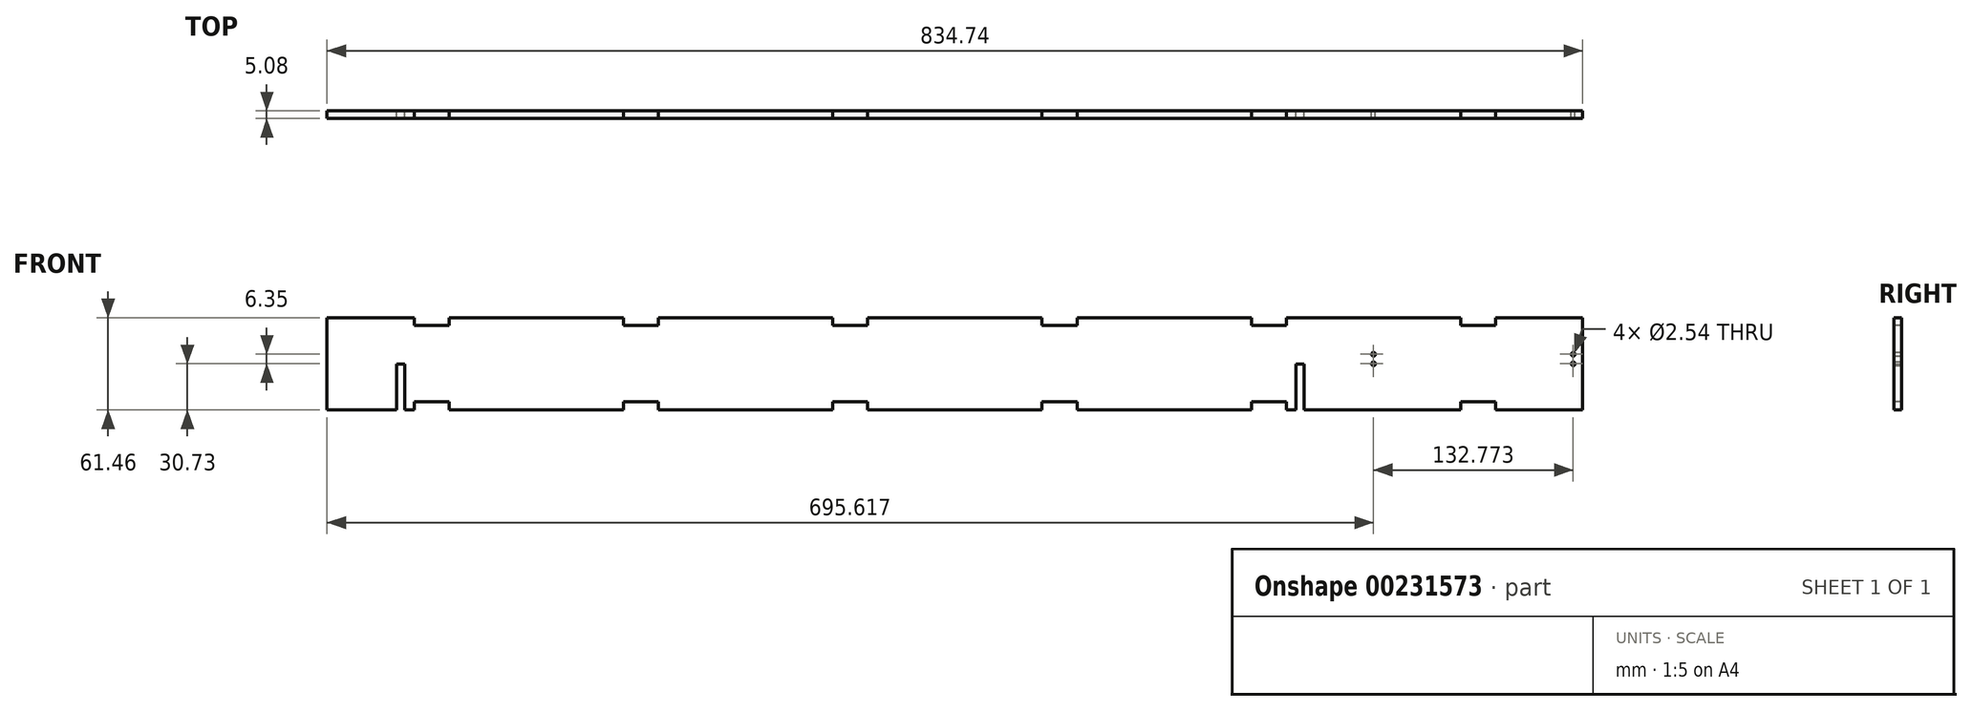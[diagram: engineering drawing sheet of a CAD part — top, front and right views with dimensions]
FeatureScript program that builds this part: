
annotation { "Feature Type Name" : "Feature", "Feature Type Description" : "" }
export const myFeature = defineFeature(function(context is Context, id is Id, definition is map)
    precondition{}
    {
        {
            var Q0;
            Q0=qCreatedBy(makeId("Front.planeOp"),FACE);
            var sketch = newSketch(context, id + "F0", { "sketchPlane" : qUnion([Q0])});
            skLineSegment(sketch, "E0.bottom", {"start": v(0, 0) * mm, "end": v(834.74, 0) * mm});
            skLineSegment(sketch, "E0.top", {"start": v(0, 50.8) * mm, "end": v(834.74, 50.8) * mm});
            skLineSegment(sketch, "E0.left", {"start": v(0, 0) * mm, "end": v(0, 50.8) * mm});
            skLineSegment(sketch, "E0.right", {"start": v(834.74, 0) * mm, "end": v(834.74, 50.8) * mm});
            skLineSegment(sketch, "E1", {"start": v(57.92, 50.8) * mm, "end": v(57.92, 0) * mm, "construction": true});
            skLineSegment(sketch, "E2", {"start": v(75.88, 50.8) * mm, "end": v(75.88, 0) * mm, "construction": true});
            skLineSegment(sketch, "E3", {"start": v(776.82, 50.8) * mm, "end": v(776.82, 0) * mm, "construction": true});
            skLineSegment(sketch, "E4", {"start": v(758.86, 50.8) * mm, "end": v(758.86, 0) * mm, "construction": true});
            skSolve(sketch);
        }
        {
            var Q0;
            Q0=makeQuery(id+"F0.imprint","IMPRINT",FACE,{"disambiguationData":[TD([[makeQuery(id+"F0.imprint","IMPRINT",EDGE,{"derivedFrom":sQuery(id+"F0.wireOp",EDGE,"E0.bottom")}),1.0]])]});
            extrude(context, id + "F1", {"entities" : qUnion([Q0]), "depth" : 5.08 * mm});
        }
        {
            var Q0;
            Q0=makeQuery(id+"F1.opExtrude","CAP_FACE",FACE,{"disambiguationData":[OSD([sQuery(id+"F0.wireOp",EDGE,"E0.bottom"),sQuery(id+"F0.wireOp",EDGE,"E0.top"),sQuery(id+"F0.wireOp",EDGE,"E0.left"),sQuery(id+"F0.wireOp",EDGE,"E0.right")])],"isStart":false});
            var sketch = newSketch(context, id + "F2", { "sketchPlane" : qUnion([Q0])});
            skLineSegment(sketch, "E5", {"start": v(57.92, 0) * mm, "end": v(57.92, 50.8) * mm});
            skLineSegment(sketch, "E6", {"start": v(81.2, 0) * mm, "end": v(81.2, 50.8) * mm});
            skLineSegment(sketch, "E7", {"start": v(776.82, 0) * mm, "end": v(776.82, 50.8) * mm});
            skLineSegment(sketch, "E8", {"start": v(753.54, 0) * mm, "end": v(753.54, 50.8) * mm});
            skLineSegment(sketch, "E9", {"start": v(197.05, 50.8) * mm, "end": v(197.05, 0) * mm});
            skLineSegment(sketch, "E10", {"start": v(220.32, 0) * mm, "end": v(220.32, 50.8) * mm});
            skLineSegment(sketch, "E11", {"start": v(336.17, 50.8) * mm, "end": v(336.17, 0) * mm});
            skLineSegment(sketch, "E12", {"start": v(359.45, 0.94) * mm, "end": v(359.45, 50.8) * mm});
            skLineSegment(sketch, "E13", {"start": v(475.3, 0) * mm, "end": v(475.3, 50.8) * mm});
            skLineSegment(sketch, "E14", {"start": v(498.57, 0) * mm, "end": v(498.57, 50.8) * mm});
            skLineSegment(sketch, "E15", {"start": v(614.42, 50.8) * mm, "end": v(614.42, 0) * mm});
            skLineSegment(sketch, "E16", {"start": v(637.7, 50.8) * mm, "end": v(637.7, 0) * mm});
            skCircle(sketch, "E17", {"center": v(9.53, 25.4) * mm, "radius": 1.27 * mm});
            skPoint(sketch, "E17.centerSnap0", {"position": v(0, 25.4) * mm});
            skCircle(sketch, "E18", {"center": v(825.22, 25.4) * mm, "radius": 1.27 * mm});
            skSolve(sketch);
        }
        {
            var Q0;
            {var subQ0=sQuery(id+"F2.wireOp",EDGE,"E6");Q0=makeQuery(id+"F2.imprint","IMPRINT",FACE,{"disambiguationData":[TD([[makeQuery(id+"F2.imprint","IMPRINT",EDGE,{"derivedFrom":subQ0}),-1.0]])]});}
            var sketch = newSketch(context, id + "F3", { "sketchPlane" : qUnion([Q0])});
            skLineSegment(sketch, "E19", {"start": v(0, 25.4) * mm, "end": v(834.74, 25.4) * mm, "construction": true});
            skLineSegment(sketch, "E20", {"start": v(0, 50.8) * mm, "end": v(0, 56.13) * mm});
            skLineSegment(sketch, "E21", {"start": v(0, 56.13) * mm, "end": v(57.92, 56.13) * mm});
            skLineSegment(sketch, "E22", {"start": v(57.92, 56.13) * mm, "end": v(57.92, 50.8) * mm});
            skLineSegment(sketch, "E23", {"start": v(81.2, 50.8) * mm, "end": v(81.2, 56.13) * mm});
            skLineSegment(sketch, "E24", {"start": v(81.2, 56.13) * mm, "end": v(197.05, 56.13) * mm});
            skLineSegment(sketch, "E25", {"start": v(197.05, 56.13) * mm, "end": v(197.05, 50.8) * mm});
            skLineSegment(sketch, "E26", {"start": v(220.32, 50.8) * mm, "end": v(220.32, 56.13) * mm});
            skLineSegment(sketch, "E27", {"start": v(220.32, 56.13) * mm, "end": v(336.17, 56.13) * mm});
            skLineSegment(sketch, "E28", {"start": v(336.17, 56.13) * mm, "end": v(336.17, 50.8) * mm});
            skLineSegment(sketch, "E29", {"start": v(359.45, 50.8) * mm, "end": v(359.45, 56.13) * mm});
            skLineSegment(sketch, "E30", {"start": v(359.45, 56.13) * mm, "end": v(475.3, 56.13) * mm});
            skLineSegment(sketch, "E31", {"start": v(475.3, 56.13) * mm, "end": v(475.3, 50.8) * mm});
            skLineSegment(sketch, "E32", {"start": v(498.57, 50.8) * mm, "end": v(498.57, 56.13) * mm});
            skLineSegment(sketch, "E33", {"start": v(498.57, 56.13) * mm, "end": v(614.42, 56.13) * mm});
            skLineSegment(sketch, "E34", {"start": v(614.42, 56.13) * mm, "end": v(614.42, 50.8) * mm});
            skLineSegment(sketch, "E35", {"start": v(637.7, 50.8) * mm, "end": v(637.7, 56.13) * mm});
            skLineSegment(sketch, "E36", {"start": v(637.7, 56.13) * mm, "end": v(753.54, 56.13) * mm});
            skLineSegment(sketch, "E37", {"start": v(753.54, 56.13) * mm, "end": v(753.54, 50.8) * mm});
            skLineSegment(sketch, "E38", {"start": v(776.82, 50.8) * mm, "end": v(776.82, 56.13) * mm});
            skLineSegment(sketch, "E39", {"start": v(776.82, 56.13) * mm, "end": v(834.74, 56.13) * mm});
            skLineSegment(sketch, "E40", {"start": v(834.74, 56.13) * mm, "end": v(834.74, 50.8) * mm});
            skLineSegment(sketch, "E41.MirrorCS", {"start": v(637.7, 0) * mm, "end": v(637.7, -5.33) * mm});
            skLineSegment(sketch, "E42.MirrorCS", {"start": v(753.54, -5.33) * mm, "end": v(753.54, 0) * mm});
            skLineSegment(sketch, "E43.MirrorCS", {"start": v(498.57, 0) * mm, "end": v(498.57, -5.33) * mm});
            skLineSegment(sketch, "E44.MirrorCS", {"start": v(57.92, -5.33) * mm, "end": v(57.92, 0) * mm});
            skLineSegment(sketch, "E45.MirrorCS", {"start": v(776.82, 0) * mm, "end": v(776.82, -5.33) * mm});
            skLineSegment(sketch, "E46.MirrorCS", {"start": v(475.3, -5.33) * mm, "end": v(475.3, 0) * mm});
            skLineSegment(sketch, "E47.MirrorCS", {"start": v(81.2, 0) * mm, "end": v(81.2, -5.33) * mm});
            skLineSegment(sketch, "E48.MirrorCS", {"start": v(197.05, -5.33) * mm, "end": v(197.05, 0) * mm});
            skLineSegment(sketch, "E49.MirrorCS", {"start": v(614.42, -5.33) * mm, "end": v(614.42, 0) * mm});
            skLineSegment(sketch, "E50.MirrorCS", {"start": v(220.32, 0) * mm, "end": v(220.32, -5.33) * mm});
            skLineSegment(sketch, "E51.MirrorCS", {"start": v(359.45, 0) * mm, "end": v(359.45, -5.33) * mm});
            skLineSegment(sketch, "E52.MirrorCS", {"start": v(336.17, -5.33) * mm, "end": v(336.17, 0) * mm});
            skLineSegment(sketch, "E53.MirrorCS", {"start": v(0, 0) * mm, "end": v(0, -5.33) * mm});
            skLineSegment(sketch, "E54.MirrorCS", {"start": v(834.74, -5.33) * mm, "end": v(834.74, 0) * mm});
            skLineSegment(sketch, "E55.MirrorCS", {"start": v(776.82, -5.33) * mm, "end": v(834.74, -5.33) * mm});
            skLineSegment(sketch, "E56.MirrorCS", {"start": v(637.7, -5.33) * mm, "end": v(753.54, -5.33) * mm});
            skLineSegment(sketch, "E57.MirrorCS", {"start": v(498.57, -5.33) * mm, "end": v(614.42, -5.33) * mm});
            skLineSegment(sketch, "E58.MirrorCS", {"start": v(0, -5.33) * mm, "end": v(57.92, -5.33) * mm});
            skLineSegment(sketch, "E59.MirrorCS", {"start": v(81.2, -5.33) * mm, "end": v(197.05, -5.33) * mm});
            skLineSegment(sketch, "E60.MirrorCS", {"start": v(220.32, -5.33) * mm, "end": v(336.17, -5.33) * mm});
            skLineSegment(sketch, "E61.MirrorCS", {"start": v(359.45, -5.33) * mm, "end": v(475.3, -5.33) * mm});
            skLineSegment(sketch, "E62", {"start": v(0, 50.8) * mm, "end": v(834.74, 50.8) * mm});
            skLineSegment(sketch, "E63", {"start": v(834.74, 0) * mm, "end": v(0, 0) * mm});
            skSolve(sketch);
        }
        {
            var Q0;
            {var subQ0=sQuery(id+"F3.wireOp",EDGE,"E20");Q0=makeQuery(id+"F3.imprint","IMPRINT",FACE,{"disambiguationData":[TD([[makeQuery(id+"F3.imprint","IMPRINT",EDGE,{"derivedFrom":subQ0}),-1.0]])]});}
            var Q1;
            {var subQ0=sQuery(id+"F3.wireOp",EDGE,"E23");Q1=makeQuery(id+"F3.imprint","IMPRINT",FACE,{"disambiguationData":[TD([[makeQuery(id+"F3.imprint","IMPRINT",EDGE,{"derivedFrom":subQ0}),-1.0]])]});}
            var Q2;
            {var subQ0=sQuery(id+"F3.wireOp",EDGE,"E44.MirrorCS");Q2=makeQuery(id+"F3.imprint","IMPRINT",FACE,{"disambiguationData":[TD([[makeQuery(id+"F3.imprint","IMPRINT",EDGE,{"derivedFrom":subQ0}),1.0]])]});}
            var Q3;
            {var subQ0=sQuery(id+"F3.wireOp",EDGE,"E47.MirrorCS");Q3=makeQuery(id+"F3.imprint","IMPRINT",FACE,{"disambiguationData":[TD([[makeQuery(id+"F3.imprint","IMPRINT",EDGE,{"derivedFrom":subQ0}),1.0]])]});}
            var Q4;
            {var subQ0=sQuery(id+"F3.wireOp",EDGE,"E26");Q4=makeQuery(id+"F3.imprint","IMPRINT",FACE,{"disambiguationData":[TD([[makeQuery(id+"F3.imprint","IMPRINT",EDGE,{"derivedFrom":subQ0}),-1.0]])]});}
            var Q5;
            {var subQ0=sQuery(id+"F3.wireOp",EDGE,"E50.MirrorCS");Q5=makeQuery(id+"F3.imprint","IMPRINT",FACE,{"disambiguationData":[TD([[makeQuery(id+"F3.imprint","IMPRINT",EDGE,{"derivedFrom":subQ0}),1.0]])]});}
            var Q6;
            {var subQ0=sQuery(id+"F3.wireOp",EDGE,"E29");Q6=makeQuery(id+"F3.imprint","IMPRINT",FACE,{"disambiguationData":[TD([[makeQuery(id+"F3.imprint","IMPRINT",EDGE,{"derivedFrom":subQ0}),-1.0]])]});}
            var Q7;
            {var subQ0=sQuery(id+"F3.wireOp",EDGE,"E46.MirrorCS");Q7=makeQuery(id+"F3.imprint","IMPRINT",FACE,{"disambiguationData":[TD([[makeQuery(id+"F3.imprint","IMPRINT",EDGE,{"derivedFrom":subQ0}),1.0]])]});}
            var Q8;
            {var subQ0=sQuery(id+"F3.wireOp",EDGE,"E32");Q8=makeQuery(id+"F3.imprint","IMPRINT",FACE,{"disambiguationData":[TD([[makeQuery(id+"F3.imprint","IMPRINT",EDGE,{"derivedFrom":subQ0}),-1.0]])]});}
            var Q9;
            {var subQ0=sQuery(id+"F3.wireOp",EDGE,"E43.MirrorCS");Q9=makeQuery(id+"F3.imprint","IMPRINT",FACE,{"disambiguationData":[TD([[makeQuery(id+"F3.imprint","IMPRINT",EDGE,{"derivedFrom":subQ0}),1.0]])]});}
            var Q10;
            {var subQ0=sQuery(id+"F3.wireOp",EDGE,"E35");Q10=makeQuery(id+"F3.imprint","IMPRINT",FACE,{"disambiguationData":[TD([[makeQuery(id+"F3.imprint","IMPRINT",EDGE,{"derivedFrom":subQ0}),-1.0]])]});}
            var Q11;
            {var subQ0=sQuery(id+"F3.wireOp",EDGE,"E41.MirrorCS");Q11=makeQuery(id+"F3.imprint","IMPRINT",FACE,{"disambiguationData":[TD([[makeQuery(id+"F3.imprint","IMPRINT",EDGE,{"derivedFrom":subQ0}),1.0]])]});}
            var Q12;
            {var subQ0=sQuery(id+"F3.wireOp",EDGE,"E38");Q12=makeQuery(id+"F3.imprint","IMPRINT",FACE,{"disambiguationData":[TD([[makeQuery(id+"F3.imprint","IMPRINT",EDGE,{"derivedFrom":subQ0}),-1.0]])]});}
            var Q13;
            {var subQ0=sQuery(id+"F3.wireOp",EDGE,"E45.MirrorCS");Q13=makeQuery(id+"F3.imprint","IMPRINT",FACE,{"disambiguationData":[TD([[makeQuery(id+"F3.imprint","IMPRINT",EDGE,{"derivedFrom":subQ0}),1.0]])]});}
            extrude(context, id + "F4", {"entities" : qUnion([Q0, Q1, Q2, Q3, Q4, Q5, Q6, Q7, Q8, Q9, Q10, Q11, Q12, Q13]), "operationType" : NewBodyOperationType.ADD, "oppositeDirection" : true, "depth" : 5.08 * mm});
        }
        {
            var Q0;
            {var subQ0=sQuery(id+"F3.wireOp",EDGE,"E63");var subQ1=sQuery(id+"F3.wireOp",EDGE,"E62");Q0=makeQuery(id+"F4.boolean.opBoolean","MERGE",FACE,{"derivedFrom":[makeQuery(id+"F1.opExtrude","CAP_FACE",FACE,{"disambiguationData":[OSD([sQuery(id+"F0.wireOp",EDGE,"E0.bottom"),sQuery(id+"F0.wireOp",EDGE,"E0.top"),sQuery(id+"F0.wireOp",EDGE,"E0.left"),sQuery(id+"F0.wireOp",EDGE,"E0.right")])],"isStart":true}),makeQuery(id+"F4.opExtrude","CAP_FACE",FACE,{"disambiguationData":[OSD([sQuery(id+"F3.wireOp",EDGE,"E20"),sQuery(id+"F3.wireOp",EDGE,"E21"),sQuery(id+"F3.wireOp",EDGE,"E22"),subQ1])],"isStart":false}),makeQuery(id+"F4.opExtrude","CAP_FACE",FACE,{"disambiguationData":[OSD([sQuery(id+"F3.wireOp",EDGE,"E23"),sQuery(id+"F3.wireOp",EDGE,"E24"),sQuery(id+"F3.wireOp",EDGE,"E25"),subQ1])],"isStart":false}),makeQuery(id+"F4.opExtrude","CAP_FACE",FACE,{"disambiguationData":[OSD([sQuery(id+"F3.wireOp",EDGE,"E26"),sQuery(id+"F3.wireOp",EDGE,"E27"),sQuery(id+"F3.wireOp",EDGE,"E28"),subQ1])],"isStart":false}),makeQuery(id+"F4.opExtrude","CAP_FACE",FACE,{"disambiguationData":[OSD([sQuery(id+"F3.wireOp",EDGE,"E29"),sQuery(id+"F3.wireOp",EDGE,"E30"),sQuery(id+"F3.wireOp",EDGE,"E31"),subQ1])],"isStart":false}),makeQuery(id+"F4.opExtrude","CAP_FACE",FACE,{"disambiguationData":[OSD([sQuery(id+"F3.wireOp",EDGE,"E32"),sQuery(id+"F3.wireOp",EDGE,"E33"),sQuery(id+"F3.wireOp",EDGE,"E34"),subQ1])],"isStart":false}),makeQuery(id+"F4.opExtrude","CAP_FACE",FACE,{"disambiguationData":[OSD([sQuery(id+"F3.wireOp",EDGE,"E35"),sQuery(id+"F3.wireOp",EDGE,"E36"),sQuery(id+"F3.wireOp",EDGE,"E37"),subQ1])],"isStart":false}),makeQuery(id+"F4.opExtrude","CAP_FACE",FACE,{"disambiguationData":[OSD([sQuery(id+"F3.wireOp",EDGE,"E38"),sQuery(id+"F3.wireOp",EDGE,"E39"),sQuery(id+"F3.wireOp",EDGE,"E40"),subQ1])],"isStart":false}),makeQuery(id+"F4.opExtrude","CAP_FACE",FACE,{"disambiguationData":[OSD([sQuery(id+"F3.wireOp",EDGE,"E41.MirrorCS"),sQuery(id+"F3.wireOp",EDGE,"E42.MirrorCS"),sQuery(id+"F3.wireOp",EDGE,"E56.MirrorCS"),subQ0])],"isStart":false}),makeQuery(id+"F4.opExtrude","CAP_FACE",FACE,{"disambiguationData":[OSD([sQuery(id+"F3.wireOp",EDGE,"E43.MirrorCS"),sQuery(id+"F3.wireOp",EDGE,"E49.MirrorCS"),sQuery(id+"F3.wireOp",EDGE,"E57.MirrorCS"),subQ0])],"isStart":false}),makeQuery(id+"F4.opExtrude","CAP_FACE",FACE,{"disambiguationData":[OSD([sQuery(id+"F3.wireOp",EDGE,"E44.MirrorCS"),sQuery(id+"F3.wireOp",EDGE,"E53.MirrorCS"),sQuery(id+"F3.wireOp",EDGE,"E58.MirrorCS"),subQ0])],"isStart":false}),makeQuery(id+"F4.opExtrude","CAP_FACE",FACE,{"disambiguationData":[OSD([sQuery(id+"F3.wireOp",EDGE,"E45.MirrorCS"),sQuery(id+"F3.wireOp",EDGE,"E54.MirrorCS"),sQuery(id+"F3.wireOp",EDGE,"E55.MirrorCS"),subQ0])],"isStart":false}),makeQuery(id+"F4.opExtrude","CAP_FACE",FACE,{"disambiguationData":[OSD([sQuery(id+"F3.wireOp",EDGE,"E46.MirrorCS"),sQuery(id+"F3.wireOp",EDGE,"E51.MirrorCS"),sQuery(id+"F3.wireOp",EDGE,"E61.MirrorCS"),subQ0])],"isStart":false}),makeQuery(id+"F4.opExtrude","CAP_FACE",FACE,{"disambiguationData":[OSD([sQuery(id+"F3.wireOp",EDGE,"E47.MirrorCS"),sQuery(id+"F3.wireOp",EDGE,"E48.MirrorCS"),sQuery(id+"F3.wireOp",EDGE,"E59.MirrorCS"),subQ0])],"isStart":false}),makeQuery(id+"F4.opExtrude","CAP_FACE",FACE,{"disambiguationData":[OSD([sQuery(id+"F3.wireOp",EDGE,"E50.MirrorCS"),sQuery(id+"F3.wireOp",EDGE,"E52.MirrorCS"),sQuery(id+"F3.wireOp",EDGE,"E60.MirrorCS"),subQ0])],"isStart":false})]});}
            var sketch = newSketch(context, id + "F5", { "sketchPlane" : qUnion([Q0])});
            skLineSegment(sketch, "E64.bottom", {"start": v(-51.57, -5.33) * mm, "end": v(-46.24, -5.33) * mm});
            skLineSegment(sketch, "E64.top", {"start": v(-51.57, 25.15) * mm, "end": v(-46.24, 25.15) * mm});
            skLineSegment(sketch, "E64.left", {"start": v(-51.57, -5.33) * mm, "end": v(-51.57, 25.15) * mm});
            skLineSegment(sketch, "E64.right", {"start": v(-46.24, -5.33) * mm, "end": v(-46.24, 25.15) * mm});
            skLineSegment(sketch, "E65.bottom", {"start": v(-649.38, -5.33) * mm, "end": v(-644.04, -5.33) * mm});
            skLineSegment(sketch, "E65.top", {"start": v(-649.38, 25.15) * mm, "end": v(-644.04, 25.15) * mm});
            skLineSegment(sketch, "E65.left", {"start": v(-649.38, -5.33) * mm, "end": v(-649.38, 25.15) * mm});
            skLineSegment(sketch, "E65.right", {"start": v(-644.04, -5.33) * mm, "end": v(-644.04, 25.15) * mm});
            skSolve(sketch);
        }
        {
            var Q0;
            Q0=makeQuery(id+"F5.imprint","IMPRINT",FACE,{"disambiguationData":[TD([[makeQuery(id+"F5.imprint","IMPRINT",EDGE,{"derivedFrom":sQuery(id+"F5.wireOp",EDGE,"E65.bottom")}),-1.0]])]});
            var Q1;
            Q1=makeQuery(id+"F5.imprint","IMPRINT",FACE,{"disambiguationData":[TD([[makeQuery(id+"F5.imprint","IMPRINT",EDGE,{"derivedFrom":sQuery(id+"F5.wireOp",EDGE,"E64.bottom")}),-1.0]])]});
            extrude(context, id + "F6", {"entities" : qUnion([Q0, Q1]), "operationType" : NewBodyOperationType.REMOVE, "oppositeDirection" : true, "depth" : 25.4 * mm});
        }
        {
            var Q0;
            {var subQ0=sQuery(id+"F3.wireOp",EDGE,"E63");var subQ1=sQuery(id+"F3.wireOp",EDGE,"E62");Q0=makeQuery(id+"F4.boolean.opBoolean","MERGE",FACE,{"derivedFrom":[makeQuery(id+"F1.opExtrude","CAP_FACE",FACE,{"disambiguationData":[OSD([sQuery(id+"F0.wireOp",EDGE,"E0.bottom"),sQuery(id+"F0.wireOp",EDGE,"E0.top"),sQuery(id+"F0.wireOp",EDGE,"E0.left"),sQuery(id+"F0.wireOp",EDGE,"E0.right")])],"isStart":true}),makeQuery(id+"F4.opExtrude","CAP_FACE",FACE,{"disambiguationData":[OSD([sQuery(id+"F3.wireOp",EDGE,"E20"),sQuery(id+"F3.wireOp",EDGE,"E21"),sQuery(id+"F3.wireOp",EDGE,"E22"),subQ1])],"isStart":false}),makeQuery(id+"F4.opExtrude","CAP_FACE",FACE,{"disambiguationData":[OSD([sQuery(id+"F3.wireOp",EDGE,"E23"),sQuery(id+"F3.wireOp",EDGE,"E24"),sQuery(id+"F3.wireOp",EDGE,"E25"),subQ1])],"isStart":false}),makeQuery(id+"F4.opExtrude","CAP_FACE",FACE,{"disambiguationData":[OSD([sQuery(id+"F3.wireOp",EDGE,"E26"),sQuery(id+"F3.wireOp",EDGE,"E27"),sQuery(id+"F3.wireOp",EDGE,"E28"),subQ1])],"isStart":false}),makeQuery(id+"F4.opExtrude","CAP_FACE",FACE,{"disambiguationData":[OSD([sQuery(id+"F3.wireOp",EDGE,"E29"),sQuery(id+"F3.wireOp",EDGE,"E30"),sQuery(id+"F3.wireOp",EDGE,"E31"),subQ1])],"isStart":false}),makeQuery(id+"F4.opExtrude","CAP_FACE",FACE,{"disambiguationData":[OSD([sQuery(id+"F3.wireOp",EDGE,"E32"),sQuery(id+"F3.wireOp",EDGE,"E33"),sQuery(id+"F3.wireOp",EDGE,"E34"),subQ1])],"isStart":false}),makeQuery(id+"F4.opExtrude","CAP_FACE",FACE,{"disambiguationData":[OSD([sQuery(id+"F3.wireOp",EDGE,"E35"),sQuery(id+"F3.wireOp",EDGE,"E36"),sQuery(id+"F3.wireOp",EDGE,"E37"),subQ1])],"isStart":false}),makeQuery(id+"F4.opExtrude","CAP_FACE",FACE,{"disambiguationData":[OSD([sQuery(id+"F3.wireOp",EDGE,"E38"),sQuery(id+"F3.wireOp",EDGE,"E39"),sQuery(id+"F3.wireOp",EDGE,"E40"),subQ1])],"isStart":false}),makeQuery(id+"F4.opExtrude","CAP_FACE",FACE,{"disambiguationData":[OSD([sQuery(id+"F3.wireOp",EDGE,"E41.MirrorCS"),sQuery(id+"F3.wireOp",EDGE,"E42.MirrorCS"),sQuery(id+"F3.wireOp",EDGE,"E56.MirrorCS"),subQ0])],"isStart":false}),makeQuery(id+"F4.opExtrude","CAP_FACE",FACE,{"disambiguationData":[OSD([sQuery(id+"F3.wireOp",EDGE,"E43.MirrorCS"),sQuery(id+"F3.wireOp",EDGE,"E49.MirrorCS"),sQuery(id+"F3.wireOp",EDGE,"E57.MirrorCS"),subQ0])],"isStart":false}),makeQuery(id+"F4.opExtrude","CAP_FACE",FACE,{"disambiguationData":[OSD([sQuery(id+"F3.wireOp",EDGE,"E44.MirrorCS"),sQuery(id+"F3.wireOp",EDGE,"E53.MirrorCS"),sQuery(id+"F3.wireOp",EDGE,"E58.MirrorCS"),subQ0])],"isStart":false}),makeQuery(id+"F4.opExtrude","CAP_FACE",FACE,{"disambiguationData":[OSD([sQuery(id+"F3.wireOp",EDGE,"E45.MirrorCS"),sQuery(id+"F3.wireOp",EDGE,"E54.MirrorCS"),sQuery(id+"F3.wireOp",EDGE,"E55.MirrorCS"),subQ0])],"isStart":false}),makeQuery(id+"F4.opExtrude","CAP_FACE",FACE,{"disambiguationData":[OSD([sQuery(id+"F3.wireOp",EDGE,"E46.MirrorCS"),sQuery(id+"F3.wireOp",EDGE,"E51.MirrorCS"),sQuery(id+"F3.wireOp",EDGE,"E61.MirrorCS"),subQ0])],"isStart":false}),makeQuery(id+"F4.opExtrude","CAP_FACE",FACE,{"disambiguationData":[OSD([sQuery(id+"F3.wireOp",EDGE,"E47.MirrorCS"),sQuery(id+"F3.wireOp",EDGE,"E48.MirrorCS"),sQuery(id+"F3.wireOp",EDGE,"E59.MirrorCS"),subQ0])],"isStart":false}),makeQuery(id+"F4.opExtrude","CAP_FACE",FACE,{"disambiguationData":[OSD([sQuery(id+"F3.wireOp",EDGE,"E50.MirrorCS"),sQuery(id+"F3.wireOp",EDGE,"E52.MirrorCS"),sQuery(id+"F3.wireOp",EDGE,"E60.MirrorCS"),subQ0])],"isStart":false})]});}
            var sketch = newSketch(context, id + "F7", { "sketchPlane" : qUnion([Q0])});
            skCircle(sketch, "E66", {"center": v(-695.62, 25.4) * mm, "radius": 1.27 * mm});
            skPoint(sketch, "E67", {"position": v(-695.62, 56.13) * mm});
            skCircle(sketch, "E68", {"center": v(-695.62, 31.75) * mm, "radius": 1.27 * mm});
            skCircle(sketch, "E69", {"center": v(-828.4, 31.75) * mm, "radius": 1.27 * mm});
            skCircle(sketch, "E70", {"center": v(-828.4, 25.4) * mm, "radius": 1.27 * mm});
            skSolve(sketch);
        }
        {
            var Q0;
            Q0 = qSketchRegion(id + "F7", true);
            extrude(context, id + "F8", {"entities" : qUnion([Q0]), "operationType" : NewBodyOperationType.REMOVE, "endBound" : BoundingType.THROUGH_ALL, "oppositeDirection" : true, "depth" : 25.4 * mm});
        }
    });
